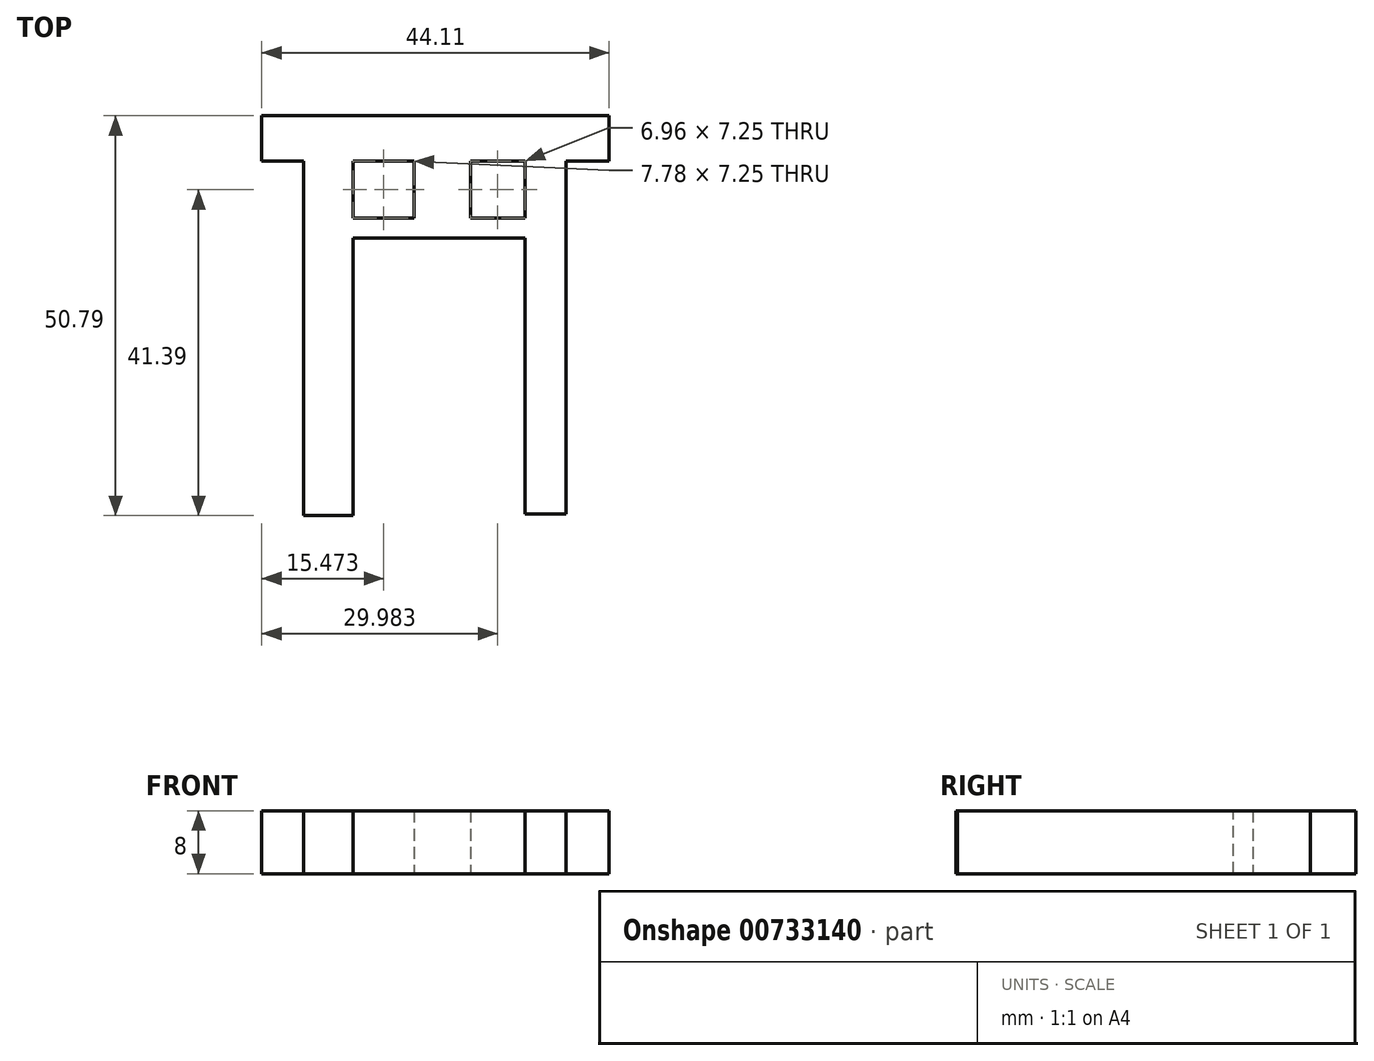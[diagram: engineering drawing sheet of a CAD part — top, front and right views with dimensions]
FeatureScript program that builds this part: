
annotation { "Feature Type Name" : "Feature", "Feature Type Description" : "" }
export const myFeature = defineFeature(function(context is Context, id is Id, definition is map)
    precondition{}
    {
        {
            var Q0;
            Q0=qCreatedBy(makeId("Top.planeOp"),FACE);
            var sketch = newSketch(context, id + "F0", { "sketchPlane" : qUnion([Q0])});
            skLineSegment(sketch, "E0.bottom", {"start": v(13.9, 17.43) * mm, "end": v(8.71, 17.43) * mm});
            skLineSegment(sketch, "E0.top", {"start": v(13.9, -32.36) * mm, "end": v(8.71, -32.36) * mm});
            skLineSegment(sketch, "E0.left", {"start": v(13.9, 17.43) * mm, "end": v(13.9, -32.36) * mm});
            skLineSegment(sketch, "E0.right", {"start": v(8.71, 17.43) * mm, "end": v(8.71, -32.36) * mm});
            skSolve(sketch);
        }
        {
            var Q0;
            Q0 = qSketchRegion(id + "F0", true);
            extrude(context, id + "F1", {"entities" : qUnion([Q0]), "depth" : 4 * mm, "offsetDistance" : 25.4 * mm});
        }
        {
            var Q0;
            Q0=qCreatedBy(makeId("Top.planeOp"),FACE);
            var sketch = newSketch(context, id + "F2", { "sketchPlane" : qUnion([Q0])});
            skLineSegment(sketch, "E1.bottom", {"start": v(-24.75, 18.2) * mm, "end": v(19.36, 18.2) * mm});
            skLineSegment(sketch, "E1.top", {"start": v(-24.75, 12.42) * mm, "end": v(19.36, 12.42) * mm});
            skLineSegment(sketch, "E1.left", {"start": v(-24.75, 18.2) * mm, "end": v(-24.75, 12.42) * mm});
            skLineSegment(sketch, "E1.right", {"start": v(19.36, 18.2) * mm, "end": v(19.36, 12.42) * mm});
            skSolve(sketch);
        }
        {
            var Q0;
            Q0 = qSketchRegion(id + "F2", true);
            extrude(context, id + "F3", {"entities" : qUnion([Q0]), "operationType" : NewBodyOperationType.ADD, "depth" : 4 * mm, "offsetDistance" : 25.4 * mm});
        }
        {
            var Q0;
            Q0=qCreatedBy(makeId("Top.planeOp"),FACE);
            var sketch = newSketch(context, id + "F4", { "sketchPlane" : qUnion([Q0])});
            skLineSegment(sketch, "E2.bottom", {"start": v(-19.42, 17.69) * mm, "end": v(-13.17, 17.69) * mm});
            skLineSegment(sketch, "E2.top", {"start": v(-19.42, -32.59) * mm, "end": v(-13.17, -32.59) * mm});
            skLineSegment(sketch, "E2.left", {"start": v(-19.42, 17.69) * mm, "end": v(-19.42, -32.59) * mm});
            skLineSegment(sketch, "E2.right", {"start": v(-13.17, 17.69) * mm, "end": v(-13.17, -32.59) * mm});
            skSolve(sketch);
        }
        {
            var Q0;
            Q0=makeQuery(id+"F4.imprint","IMPRINT",FACE,{"disambiguationData":[TD([[makeQuery(id+"F4.imprint","IMPRINT",EDGE,{"derivedFrom":sQuery(id+"F4.wireOp",EDGE,"E2.bottom")}),-1.0]])]});
            extrude(context, id + "F5", {"entities" : qUnion([Q0]), "operationType" : NewBodyOperationType.ADD, "depth" : 4 * mm, "offsetDistance" : 25.4 * mm});
        }
        {
            var Q0;
            Q0=qCreatedBy(makeId("Top.planeOp"),FACE);
            var sketch = newSketch(context, id + "F6", { "sketchPlane" : qUnion([Q0])});
            skLineSegment(sketch, "E3.bottom", {"start": v(-19.38, 5.18) * mm, "end": v(13.85, 5.18) * mm});
            skLineSegment(sketch, "E3.top", {"start": v(-19.38, 2.67) * mm, "end": v(13.85, 2.67) * mm});
            skLineSegment(sketch, "E3.left", {"start": v(-19.38, 5.18) * mm, "end": v(-19.38, 2.67) * mm});
            skLineSegment(sketch, "E3.right", {"start": v(13.85, 5.18) * mm, "end": v(13.85, 2.67) * mm});
            skSolve(sketch);
        }
        {
            var Q0;
            Q0=makeQuery(id+"F6.imprint","IMPRINT",FACE,{"disambiguationData":[TD([[makeQuery(id+"F6.imprint","IMPRINT",EDGE,{"derivedFrom":sQuery(id+"F6.wireOp",EDGE,"E3.bottom")}),-1.0]])]});
            extrude(context, id + "F7", {"entities" : qUnion([Q0]), "operationType" : NewBodyOperationType.ADD, "depth" : 4 * mm, "offsetDistance" : 25.4 * mm});
        }
        {
            var Q0;
            Q0=makeQuery(id+"F7.opExtrude","CAP_FACE",FACE,{"disambiguationData":[OSD([sQuery(id+"F6.wireOp",EDGE,"E3.bottom"),sQuery(id+"F6.wireOp",EDGE,"E3.top"),sQuery(id+"F6.wireOp",EDGE,"E3.left"),sQuery(id+"F6.wireOp",EDGE,"E3.right")])],"isStart":false});
            extrude(context, id + "F8", {"entities" : qUnion([Q0]), "operationType" : NewBodyOperationType.ADD, "depth" : 4 * mm, "offsetDistance" : 25.4 * mm});
        }
        {
            var Q0;
            Q0=qCreatedBy(makeId("Top.planeOp"),FACE);
            var sketch = newSketch(context, id + "F9", { "sketchPlane" : qUnion([Q0])});
            skLineSegment(sketch, "E4.bottom", {"start": v(-5.39, 12.45) * mm, "end": v(1.75, 12.45) * mm});
            skLineSegment(sketch, "E4.top", {"start": v(-5.39, 4.37) * mm, "end": v(1.75, 4.37) * mm});
            skLineSegment(sketch, "E4.left", {"start": v(-5.39, 12.45) * mm, "end": v(-5.39, 4.37) * mm});
            skLineSegment(sketch, "E4.right", {"start": v(1.75, 12.45) * mm, "end": v(1.75, 4.37) * mm});
            skSolve(sketch);
        }
        {
            var Q0;
            Q0 = qSketchRegion(id + "F9", true);
            extrude(context, id + "F10", {"entities" : qUnion([Q0]), "operationType" : NewBodyOperationType.ADD, "depth" : 8 * mm, "offsetDistance" : 25.4 * mm});
        }
    });
